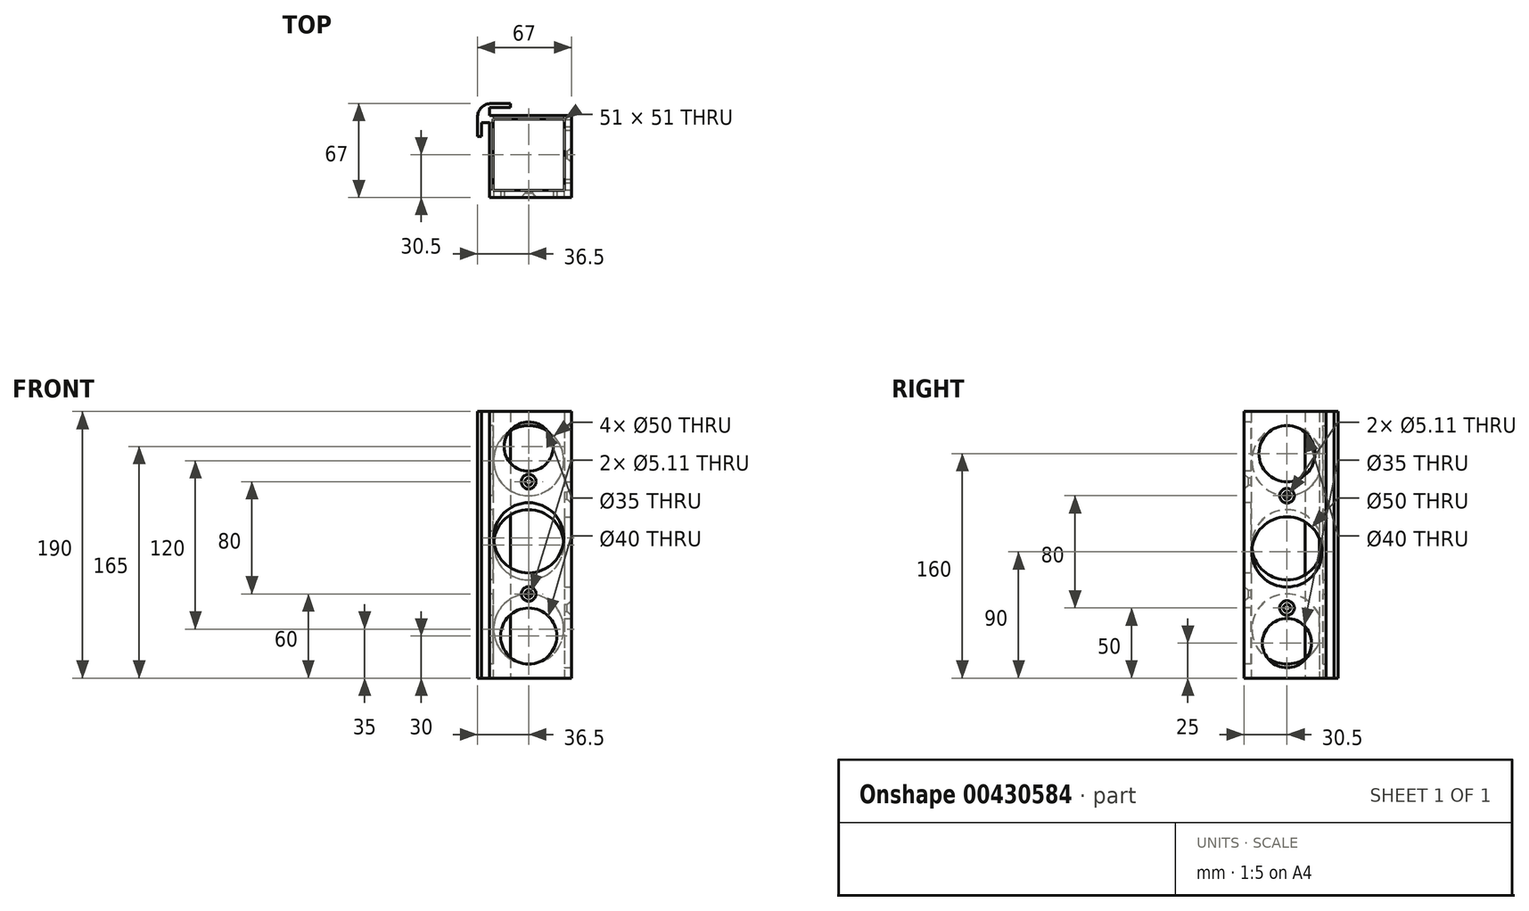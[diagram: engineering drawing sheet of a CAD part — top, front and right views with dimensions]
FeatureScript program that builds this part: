
annotation { "Feature Type Name" : "Feature", "Feature Type Description" : "" }
export const myFeature = defineFeature(function(context is Context, id is Id, definition is map)
    precondition{}
    {
        {
            var Q0;
            Q0=qCreatedBy(makeId("Top.planeOp"),FACE);
            var sketch = newSketch(context, id + "F0", { "sketchPlane" : qUnion([Q0])});
            skLineSegment(sketch, "E0.bottom", {"start": v(25.5, -25.5) * mm, "end": v(-25.5, -25.5) * mm});
            skLineSegment(sketch, "E0.top", {"start": v(25.5, 25.5) * mm, "end": v(-25.5, 25.5) * mm});
            skLineSegment(sketch, "E0.left", {"start": v(25.5, -25.5) * mm, "end": v(25.5, 25.5) * mm});
            skLineSegment(sketch, "E0.right", {"start": v(-25.5, -25.5) * mm, "end": v(-25.5, 25.5) * mm});
            skPoint(sketch, "E0.middle", {"position": v(0, 0) * mm});
            skLineSegment(sketch, "E1.bottom", {"start": v(-28, 28) * mm, "end": v(30.5, 28) * mm});
            skLineSegment(sketch, "E1.top", {"start": v(-28, -30.5) * mm, "end": v(30.5, -30.5) * mm});
            skLineSegment(sketch, "E1.left", {"start": v(-28, 28) * mm, "end": v(-28, -30.5) * mm});
            skLineSegment(sketch, "E1.right", {"start": v(30.5, 28) * mm, "end": v(30.5, -30.5) * mm});
            skLineSegment(sketch, "E2.bottom", {"start": v(-28, 28) * mm, "end": v(-23, 28) * mm});
            skLineSegment(sketch, "E2.top", {"start": v(-28, 33.5) * mm, "end": v(-23, 33.5) * mm});
            skLineSegment(sketch, "E2.left", {"start": v(-28, 28) * mm, "end": v(-28, 33.5) * mm});
            skLineSegment(sketch, "E2.right", {"start": v(-23, 28) * mm, "end": v(-23, 33.5) * mm});
            skLineSegment(sketch, "E3.bottom", {"start": v(-28, 28) * mm, "end": v(-33.5, 28) * mm});
            skLineSegment(sketch, "E3.top", {"start": v(-28, 23) * mm, "end": v(-33.5, 23) * mm});
            skLineSegment(sketch, "E3.left", {"start": v(-28, 28) * mm, "end": v(-28, 23) * mm});
            skLineSegment(sketch, "E3.right", {"start": v(-33.5, 28) * mm, "end": v(-33.5, 23) * mm});
            skLineSegment(sketch, "E4.bottom", {"start": v(-33.5, 28) * mm, "end": v(-36.5, 28) * mm});
            skLineSegment(sketch, "E4.top", {"start": v(-33.5, 13) * mm, "end": v(-36.5, 13) * mm});
            skLineSegment(sketch, "E4.left", {"start": v(-33.5, 28) * mm, "end": v(-33.5, 13) * mm});
            skLineSegment(sketch, "E4.right", {"start": v(-36.5, 28) * mm, "end": v(-36.5, 13) * mm});
            skLineSegment(sketch, "E5.bottom", {"start": v(-28, 33.5) * mm, "end": v(-13, 33.5) * mm});
            skLineSegment(sketch, "E5.top", {"start": v(-28, 36.5) * mm, "end": v(-13, 36.5) * mm});
            skLineSegment(sketch, "E5.left", {"start": v(-28, 33.5) * mm, "end": v(-28, 36.5) * mm});
            skLineSegment(sketch, "E5.right", {"start": v(-13, 33.5) * mm, "end": v(-13, 36.5) * mm});
            skLineSegment(sketch, "E6.bottom", {"start": v(-28, 28) * mm, "end": v(-36.5, 28) * mm});
            skLineSegment(sketch, "E6.top", {"start": v(-28, 36.5) * mm, "end": v(-36.5, 36.5) * mm});
            skLineSegment(sketch, "E6.left", {"start": v(-28, 28) * mm, "end": v(-28, 36.5) * mm});
            skLineSegment(sketch, "E6.right", {"start": v(-36.5, 28) * mm, "end": v(-36.5, 36.5) * mm});
            skSolve(sketch);
        }
        {
            var Q0;
            {var subQ4=sQuery(id+"F0.wireOp",EDGE,"E6.top");Q0=makeQuery(id+"F0.imprint","IMPRINT",FACE,{"disambiguationData":[TD([[makeQuery(id+"F0.imprint","IMPRINT",EDGE,{"derivedFrom":subQ4}),1.0]])]});}
            var Q1;
            {var subQ1=sQuery(id+"F0.wireOp",EDGE,"E5.top");Q1=makeQuery(id+"F0.imprint","IMPRINT",FACE,{"disambiguationData":[TD([[makeQuery(id+"F0.imprint","IMPRINT",EDGE,{"derivedFrom":subQ1}),-1.0]])]});}
            var Q2;
            {var subQ0=sQuery(id+"F0.wireOp",EDGE,"E2.bottom");Q2=makeQuery(id+"F0.imprint","IMPRINT",FACE,{"disambiguationData":[TD([[makeQuery(id+"F0.imprint","IMPRINT",EDGE,{"derivedFrom":subQ0}),1.0]])]});}
            var Q3;
            {var subQ0=sQuery(id+"F0.wireOp",EDGE,"E3.top");Q3=makeQuery(id+"F0.imprint","IMPRINT",FACE,{"disambiguationData":[TD([[makeQuery(id+"F0.imprint","IMPRINT",EDGE,{"derivedFrom":subQ0}),-1.0]])]});}
            var Q4;
            {var subQ3=sQuery(id+"F0.wireOp",EDGE,"E4.top");Q4=makeQuery(id+"F0.imprint","IMPRINT",FACE,{"disambiguationData":[TD([[makeQuery(id+"F0.imprint","IMPRINT",EDGE,{"derivedFrom":subQ3}),-1.0]])]});}
            var Q5;
            Q5=makeQuery(id+"F0.imprint","IMPRINT",FACE,{"disambiguationData":[TD([[makeQuery(id+"F0.imprint","IMPRINT",EDGE,{"derivedFrom":sQuery(id+"F0.wireOp",EDGE,"E0.bottom")}),1.0]])]});
            extrude(context, id + "F1", {"entities" : qUnion([Q0, Q1, Q2, Q3, Q4, Q5]), "depth" : 190 * mm, "offsetDistance" : 25 * mm});
        }
        {
            var Q0;
            Q0=makeQuery(id+"F1.opExtrude","SWEPT_EDGE",EDGE,{"disambiguationData":[OSD([sQuery(id+"F0.wireOp",EDGE,"E6.top"),sQuery(id+"F0.wireOp",EDGE,"E6.right")])]});
            fillet(context, id + "F2", {"entities" : qUnion([Q0]), "radius" : 10 * mm, "tangentPropagation" : true, "allowEdgeOverflow" : false});
        }
        {
            var Q0;
            Q0=makeQuery(id+"F1.opExtrude","SWEPT_FACE",FACE,{"disambiguationData":[OSD([sQuery(id+"F0.wireOp",EDGE,"E1.top")])]});
            var sketch = newSketch(context, id + "F3", { "sketchPlane" : qUnion([Q0])});
            skPoint(sketch, "E7", {"position": v(0, 140) * mm});
            skPoint(sketch, "E8", {"position": v(0, 60) * mm});
            skCircle(sketch, "E9", {"center": v(0, 100) * mm, "radius": 25 * mm});
            skCircle(sketch, "E10", {"center": v(0, 165) * mm, "radius": 17.5 * mm});
            skCircle(sketch, "E11", {"center": v(0, 30) * mm, "radius": 20 * mm});
            skSolve(sketch);
        }
        {
            var Q0;
            Q0=makeQuery(id+"F3.imprint","IMPRINT",FACE,{"disambiguationData":[TD([[makeQuery(id+"F3.imprint","IMPRINT",EDGE,{"derivedFrom":sQuery(id+"F3.wireOp",EDGE,"E9")}),1.0]])]});
            var Q1;
            Q1=makeQuery(id+"F3.imprint","IMPRINT",FACE,{"disambiguationData":[TD([[makeQuery(id+"F3.imprint","IMPRINT",EDGE,{"derivedFrom":sQuery(id+"F3.wireOp",EDGE,"E10")}),1.0]])]});
            var Q2;
            Q2=makeQuery(id+"F3.imprint","IMPRINT",FACE,{"disambiguationData":[TD([[makeQuery(id+"F3.imprint","IMPRINT",EDGE,{"derivedFrom":sQuery(id+"F3.wireOp",EDGE,"E11")}),1.0]])]});
            extrude(context, id + "F4", {"entities" : qUnion([Q0, Q1, Q2]), "operationType" : NewBodyOperationType.REMOVE, "endBound" : BoundingType.UP_TO_NEXT, "oppositeDirection" : true, "depth" : 25 * mm, "offsetDistance" : 25 * mm});
        }
        {
            var Q0;
            Q0=sQuery(id+"F3.wireOp",VERTEX,"E7");
            var Q1;
            Q1=sQuery(id+"F3.wireOp",VERTEX,"E8");
            var Q2;
            Q2=makeQuery(id+"F1.opExtrude","SWEPT_BODY",BODY,{"disambiguationData":[OSD([sQuery(id+"F0.wireOp",EDGE,"E0.bottom"),sQuery(id+"F0.wireOp",EDGE,"E0.top"),sQuery(id+"F0.wireOp",EDGE,"E0.left"),sQuery(id+"F0.wireOp",EDGE,"E0.right"),sQuery(id+"F0.wireOp",EDGE,"E1.bottom"),sQuery(id+"F0.wireOp",EDGE,"E1.top"),sQuery(id+"F0.wireOp",EDGE,"E1.left"),sQuery(id+"F0.wireOp",EDGE,"E1.right"),sQuery(id+"F0.wireOp",EDGE,"E2.right"),sQuery(id+"F0.wireOp",EDGE,"E3.top"),sQuery(id+"F0.wireOp",EDGE,"E4.top"),sQuery(id+"F0.wireOp",EDGE,"E4.left"),sQuery(id+"F0.wireOp",EDGE,"E4.right"),sQuery(id+"F0.wireOp",EDGE,"E5.bottom"),sQuery(id+"F0.wireOp",EDGE,"E5.top"),sQuery(id+"F0.wireOp",EDGE,"E5.right"),sQuery(id+"F0.wireOp",EDGE,"E6.top"),sQuery(id+"F0.wireOp",EDGE,"E6.right")])]});
            hole(context, id + "F5", {"style" : HoleStyle.C_SINK, "endStyle" : HoleEndStyle.BLIND, "standardTappedOrClearance" : lookupTablePath({ "standard" : "ANSI", "fit" : "Normal (ASME)", "size" : "#10", "type" : "Clearance" }), "standardBlindInLast" : lookupTablePath({ "fit" : "Free", "standard" : "ANSI", "size" : "#10", "type" : "Clearance" }), "holeDiameter" : 5.1 * mm, "cSinkDiameter" : 10.44 * mm, "cSinkAngle" : 82 * degree, "holeDepth" : 12 * mm, "isTappedThrough" : true, "tappedDepth" : 12 * mm, "tapClearance" : 3, "locations" : qUnion([Q0, Q1]), "scope" : qUnion([Q2])});
        }
        {
            var Q0;
            Q0=makeQuery(id+"F1.opExtrude","SWEPT_FACE",FACE,{"disambiguationData":[OSD([sQuery(id+"F0.wireOp",EDGE,"E1.right")])]});
            var sketch = newSketch(context, id + "F6", { "sketchPlane" : qUnion([Q0])});
            skPoint(sketch, "E12", {"position": v(0, 130) * mm});
            skPoint(sketch, "E13", {"position": v(0, 50) * mm});
            skCircle(sketch, "E14", {"center": v(0, 160) * mm, "radius": 20 * mm});
            skCircle(sketch, "E15", {"center": v(0, 90) * mm, "radius": 25 * mm});
            skCircle(sketch, "E16", {"center": v(0, 25) * mm, "radius": 17.5 * mm});
            skSolve(sketch);
        }
        {
            var Q0;
            Q0=sQuery(id+"F6.wireOp",VERTEX,"E12");
            var Q1;
            Q1=sQuery(id+"F6.wireOp",VERTEX,"E13");
            var Q2;
            Q2=makeQuery(id+"F1.opExtrude","SWEPT_BODY",BODY,{"disambiguationData":[OSD([sQuery(id+"F0.wireOp",EDGE,"E0.bottom"),sQuery(id+"F0.wireOp",EDGE,"E0.top"),sQuery(id+"F0.wireOp",EDGE,"E0.left"),sQuery(id+"F0.wireOp",EDGE,"E0.right"),sQuery(id+"F0.wireOp",EDGE,"E1.bottom"),sQuery(id+"F0.wireOp",EDGE,"E1.top"),sQuery(id+"F0.wireOp",EDGE,"E1.left"),sQuery(id+"F0.wireOp",EDGE,"E1.right"),sQuery(id+"F0.wireOp",EDGE,"E2.right"),sQuery(id+"F0.wireOp",EDGE,"E3.top"),sQuery(id+"F0.wireOp",EDGE,"E4.top"),sQuery(id+"F0.wireOp",EDGE,"E4.left"),sQuery(id+"F0.wireOp",EDGE,"E4.right"),sQuery(id+"F0.wireOp",EDGE,"E5.bottom"),sQuery(id+"F0.wireOp",EDGE,"E5.top"),sQuery(id+"F0.wireOp",EDGE,"E5.right"),sQuery(id+"F0.wireOp",EDGE,"E6.top"),sQuery(id+"F0.wireOp",EDGE,"E6.right")])]});
            hole(context, id + "F7", {"style" : HoleStyle.C_SINK, "endStyle" : HoleEndStyle.BLIND, "standardTappedOrClearance" : lookupTablePath({ "standard" : "ANSI", "fit" : "Normal (ASME)", "size" : "#10", "type" : "Clearance" }), "standardBlindInLast" : lookupTablePath({ "fit" : "Free", "standard" : "ANSI", "size" : "#10", "type" : "Clearance" }), "holeDiameter" : 5.1 * mm, "cSinkDiameter" : 10.44 * mm, "cSinkAngle" : 82 * degree, "holeDepth" : 12 * mm, "isTappedThrough" : true, "tappedDepth" : 12 * mm, "tapClearance" : 3, "locations" : qUnion([Q0, Q1]), "scope" : qUnion([Q2])});
        }
        {
            var Q0;
            Q0=makeQuery(id+"F6.imprint","IMPRINT",FACE,{"disambiguationData":[TD([[makeQuery(id+"F6.imprint","IMPRINT",EDGE,{"derivedFrom":sQuery(id+"F6.wireOp",EDGE,"E14")}),1.0]])]});
            var Q1;
            Q1=makeQuery(id+"F6.imprint","IMPRINT",FACE,{"disambiguationData":[TD([[makeQuery(id+"F6.imprint","IMPRINT",EDGE,{"derivedFrom":sQuery(id+"F6.wireOp",EDGE,"E15")}),1.0]])]});
            var Q2;
            Q2=makeQuery(id+"F6.imprint","IMPRINT",FACE,{"disambiguationData":[TD([[makeQuery(id+"F6.imprint","IMPRINT",EDGE,{"derivedFrom":sQuery(id+"F6.wireOp",EDGE,"E16")}),1.0]])]});
            extrude(context, id + "F8", {"entities" : qUnion([Q0, Q1, Q2]), "operationType" : NewBodyOperationType.REMOVE, "endBound" : BoundingType.UP_TO_NEXT, "oppositeDirection" : true, "depth" : 25 * mm, "offsetDistance" : 25 * mm});
        }
        {
            var Q0;
            Q0=makeQuery(id+"F1.opExtrude","SWEPT_FACE",FACE,{"disambiguationData":[OSD([sQuery(id+"F0.wireOp",EDGE,"E1.left")])]});
            var sketch = newSketch(context, id + "F9", { "sketchPlane" : qUnion([Q0])});
            skCircle(sketch, "E17", {"center": v(0, 95) * mm, "radius": 25 * mm});
            skCircle(sketch, "E18", {"center": v(0, 155) * mm, "radius": 25 * mm});
            skCircle(sketch, "E19", {"center": v(0, 35) * mm, "radius": 25 * mm});
            skSolve(sketch);
        }
        {
            var Q0;
            {var subQ0=sQuery(id+"F9.wireOp",EDGE,"E18");var subQ1=makeQuery(id+"F1.opExtrude","SWEPT_EDGE",EDGE,{"disambiguationData":[OSD([sQuery(id+"F0.wireOp",EDGE,"E1.left"),sQuery(id+"F0.wireOp",EDGE,"E3.top"),sQuery(id+"F0.wireOp",EDGE,"E3.left")])]});var subQ2=makeQuery(id+"F9.imprint","INTERSECT",VERTEX,{"disambiguationData":[OD(0.0)],"derivedFrom":[subQ1,subQ0]});Q0=makeQuery(id+"F9.imprint","IMPRINT",FACE,{"disambiguationData":[TD([[makeQuery(id+"F9.imprint","IMPRINT",EDGE,{"disambiguationData":[TD([[subQ2,1.0]])],"derivedFrom":subQ0}),1.0]])]});}
            var Q1;
            {var subQ0=sQuery(id+"F9.wireOp",EDGE,"E17");var subQ1=makeQuery(id+"F1.opExtrude","SWEPT_EDGE",EDGE,{"disambiguationData":[OSD([sQuery(id+"F0.wireOp",EDGE,"E1.left"),sQuery(id+"F0.wireOp",EDGE,"E3.top"),sQuery(id+"F0.wireOp",EDGE,"E3.left")])]});var subQ2=makeQuery(id+"F9.imprint","INTERSECT",VERTEX,{"disambiguationData":[OD(0.0)],"derivedFrom":[subQ1,subQ0]});Q1=makeQuery(id+"F9.imprint","IMPRINT",FACE,{"disambiguationData":[TD([[makeQuery(id+"F9.imprint","IMPRINT",EDGE,{"disambiguationData":[TD([[subQ2,1.0]])],"derivedFrom":subQ0}),1.0]])]});}
            var Q2;
            {var subQ0=sQuery(id+"F9.wireOp",EDGE,"E19");var subQ1=makeQuery(id+"F1.opExtrude","SWEPT_EDGE",EDGE,{"disambiguationData":[OSD([sQuery(id+"F0.wireOp",EDGE,"E1.left"),sQuery(id+"F0.wireOp",EDGE,"E3.top"),sQuery(id+"F0.wireOp",EDGE,"E3.left")])]});var subQ2=makeQuery(id+"F9.imprint","INTERSECT",VERTEX,{"disambiguationData":[OD(0.0)],"derivedFrom":[subQ1,subQ0]});Q2=makeQuery(id+"F9.imprint","IMPRINT",FACE,{"disambiguationData":[TD([[makeQuery(id+"F9.imprint","IMPRINT",EDGE,{"disambiguationData":[TD([[subQ2,-1.0]])],"derivedFrom":subQ0}),1.0]])]});}
            extrude(context, id + "F10", {"entities" : qUnion([Q0, Q1, Q2]), "operationType" : NewBodyOperationType.REMOVE, "endBound" : BoundingType.UP_TO_NEXT, "oppositeDirection" : true, "depth" : 25 * mm, "offsetDistance" : 25 * mm});
        }
        {
            var Q0;
            Q0=makeQuery(id+"F1.opExtrude","SWEPT_FACE",FACE,{"disambiguationData":[OSD([sQuery(id+"F0.wireOp",EDGE,"E1.bottom")])]});
            var sketch = newSketch(context, id + "F11", { "sketchPlane" : qUnion([Q0])});
            skCircle(sketch, "E20", {"center": v(0, 95) * mm, "radius": 25 * mm});
            skCircle(sketch, "E21", {"center": v(0, 155) * mm, "radius": 25 * mm});
            skCircle(sketch, "E22", {"center": v(0, 35) * mm, "radius": 25 * mm});
            skSolve(sketch);
        }
        {
            var Q0;
            {var subQ0=sQuery(id+"F11.wireOp",EDGE,"E21");var subQ1=makeQuery(id+"F1.opExtrude","SWEPT_EDGE",EDGE,{"disambiguationData":[OSD([sQuery(id+"F0.wireOp",EDGE,"E1.bottom"),sQuery(id+"F0.wireOp",EDGE,"E2.bottom"),sQuery(id+"F0.wireOp",EDGE,"E2.right")])]});var subQ2=makeQuery(id+"F11.imprint","INTERSECT",VERTEX,{"disambiguationData":[OD(0.0)],"derivedFrom":[subQ1,subQ0]});Q0=makeQuery(id+"F11.imprint","IMPRINT",FACE,{"disambiguationData":[TD([[makeQuery(id+"F11.imprint","IMPRINT",EDGE,{"disambiguationData":[TD([[subQ2,-1.0]])],"derivedFrom":subQ0}),1.0]])]});}
            var Q1;
            {var subQ0=sQuery(id+"F11.wireOp",EDGE,"E20");var subQ1=makeQuery(id+"F1.opExtrude","SWEPT_EDGE",EDGE,{"disambiguationData":[OSD([sQuery(id+"F0.wireOp",EDGE,"E1.bottom"),sQuery(id+"F0.wireOp",EDGE,"E2.bottom"),sQuery(id+"F0.wireOp",EDGE,"E2.right")])]});var subQ2=makeQuery(id+"F11.imprint","INTERSECT",VERTEX,{"disambiguationData":[OD(0.0)],"derivedFrom":[subQ1,subQ0]});Q1=makeQuery(id+"F11.imprint","IMPRINT",FACE,{"disambiguationData":[TD([[makeQuery(id+"F11.imprint","IMPRINT",EDGE,{"disambiguationData":[TD([[subQ2,-1.0]])],"derivedFrom":subQ0}),1.0]])]});}
            var Q2;
            {var subQ0=sQuery(id+"F11.wireOp",EDGE,"E22");var subQ1=makeQuery(id+"F1.opExtrude","SWEPT_EDGE",EDGE,{"disambiguationData":[OSD([sQuery(id+"F0.wireOp",EDGE,"E1.bottom"),sQuery(id+"F0.wireOp",EDGE,"E2.bottom"),sQuery(id+"F0.wireOp",EDGE,"E2.right")])]});var subQ2=makeQuery(id+"F11.imprint","INTERSECT",VERTEX,{"disambiguationData":[OD(0.0)],"derivedFrom":[subQ1,subQ0]});Q2=makeQuery(id+"F11.imprint","IMPRINT",FACE,{"disambiguationData":[TD([[makeQuery(id+"F11.imprint","IMPRINT",EDGE,{"disambiguationData":[TD([[subQ2,1.0]])],"derivedFrom":subQ0}),1.0]])]});}
            extrude(context, id + "F12", {"entities" : qUnion([Q0, Q1, Q2]), "operationType" : NewBodyOperationType.REMOVE, "endBound" : BoundingType.UP_TO_NEXT, "oppositeDirection" : true, "depth" : 25 * mm, "offsetDistance" : 25 * mm});
        }
    });
